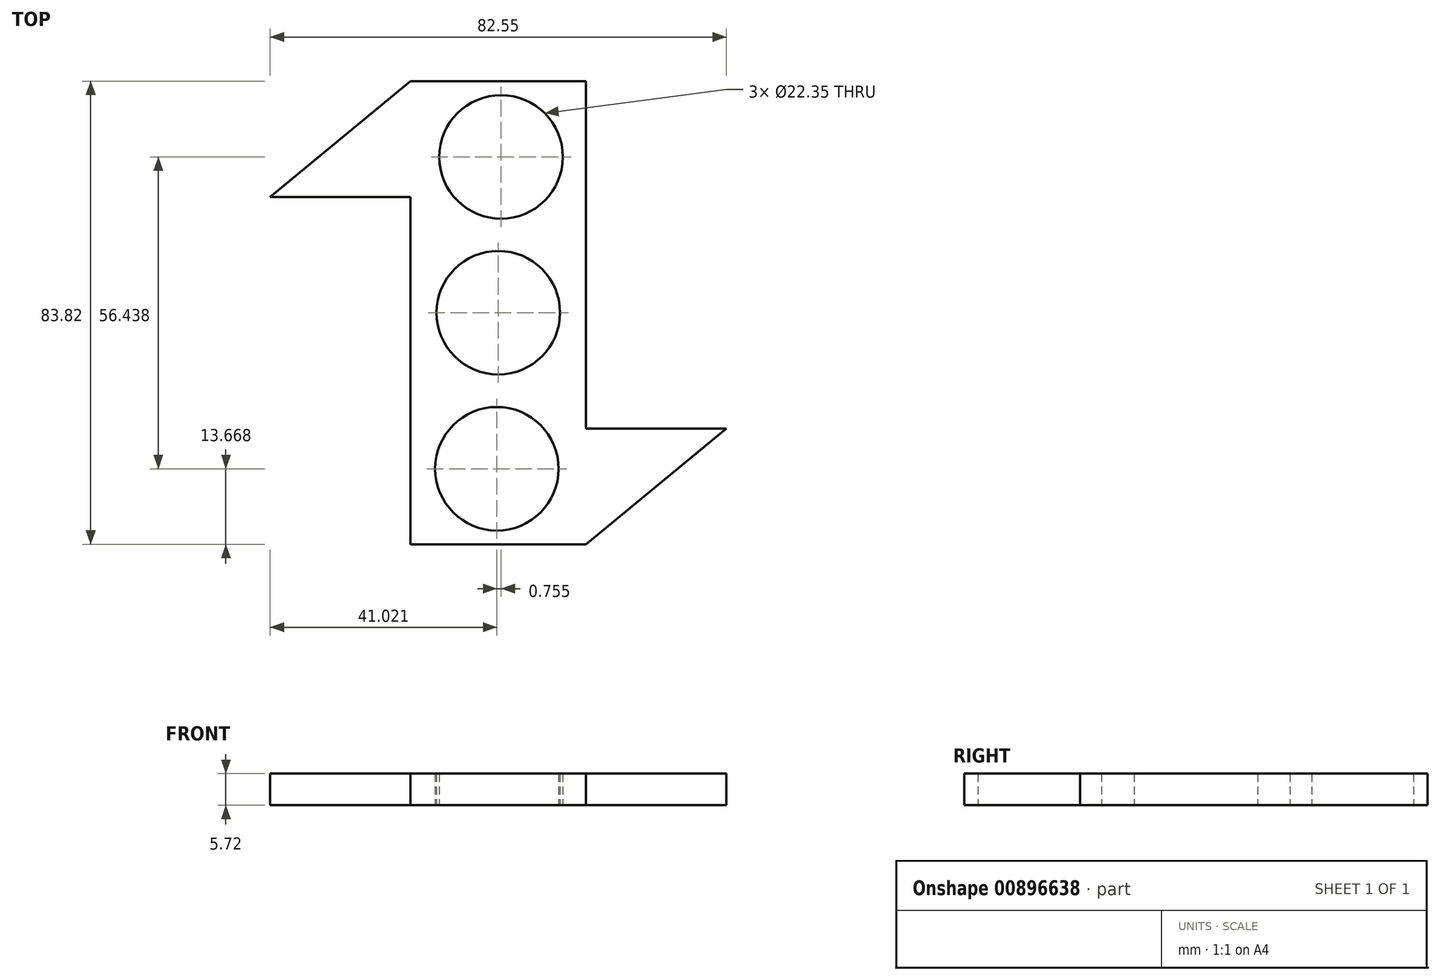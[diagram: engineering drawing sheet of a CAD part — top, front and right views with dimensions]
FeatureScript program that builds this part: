
annotation { "Feature Type Name" : "Feature", "Feature Type Description" : "" }
export const myFeature = defineFeature(function(context is Context, id is Id, definition is map)
    precondition{}
    {
        {
            var Q0;
            Q0=qCreatedBy(makeId("Top.planeOp"),FACE);
            var sketch = newSketch(context, id + "F0", { "sketchPlane" : qUnion([Q0])});
            skCircle(sketch, "E0", {"center": v(-1.1, 0.58) * mm, "radius": 11.18 * mm});
            skCircle(sketch, "E1", {"center": v(-1.1, 0.58) * mm, "radius": 15.88 * mm});
            skLineSegment(sketch, "E2", {"start": v(-16.98, 0.58) * mm, "end": v(-16.98, -41.33) * mm});
            skLineSegment(sketch, "E3", {"start": v(14.77, 0.58) * mm, "end": v(14.77, -41.33) * mm});
            skLineSegment(sketch, "E4", {"start": v(14.77, -41.33) * mm, "end": v(-16.98, -41.33) * mm});
            skLineSegment(sketch, "E5", {"start": v(-16.98, 0.58) * mm, "end": v(-16.98, 42.5) * mm});
            skLineSegment(sketch, "E6", {"start": v(14.77, 0.58) * mm, "end": v(14.77, 42.5) * mm});
            skLineSegment(sketch, "E7", {"start": v(14.77, 42.5) * mm, "end": v(-16.98, 42.5) * mm});
            skCircle(sketch, "E8", {"center": v(-0.6, 28.78) * mm, "radius": 11.18 * mm});
            skCircle(sketch, "E9", {"center": v(-1.36, -27.66) * mm, "radius": 11.18 * mm});
            skLineSegment(sketch, "E10", {"start": v(14.77, -41.33) * mm, "end": v(40.17, -20.37) * mm});
            skPoint(sketch, "E10.endSnap0", {"position": v(14.77, -20.37) * mm});
            skLineSegment(sketch, "E11", {"start": v(40.17, -20.37) * mm, "end": v(14.77, -20.37) * mm});
            skLineSegment(sketch, "E12", {"start": v(-16.98, 42.5) * mm, "end": v(-42.38, 21.54) * mm});
            skPoint(sketch, "E12.endSnap0", {"position": v(14.77, 21.54) * mm});
            skLineSegment(sketch, "E13", {"start": v(-42.38, 21.54) * mm, "end": v(-16.98, 21.54) * mm});
            skSolve(sketch);
        }
        {
            var Q0;
            {var subQ1=sQuery(id+"F0.wireOp",EDGE,"E2");Q0=makeQuery(id+"F0.imprint","IMPRINT",FACE,{"disambiguationData":[TD([[makeQuery(id+"F0.imprint","IMPRINT",EDGE,{"derivedFrom":subQ1}),1.0]])]});}
            var Q1;
            Q1=makeQuery(id+"F0.imprint","IMPRINT",FACE,{"disambiguationData":[TD([[makeQuery(id+"F0.imprint","IMPRINT",EDGE,{"derivedFrom":sQuery(id+"F0.wireOp",EDGE,"E0")}),-1.0]])]});
            var Q2;
            {var subQ1=sQuery(id+"F0.wireOp",EDGE,"E5");Q2=makeQuery(id+"F0.imprint","IMPRINT",FACE,{"disambiguationData":[TD([[makeQuery(id+"F0.imprint","IMPRINT",EDGE,{"derivedFrom":subQ1}),-1.0]])]});}
            var Q3;
            {var subQ0=sQuery(id+"F0.wireOp",EDGE,"E10");Q3=makeQuery(id+"F0.imprint","IMPRINT",FACE,{"disambiguationData":[TD([[makeQuery(id+"F0.imprint","IMPRINT",EDGE,{"derivedFrom":subQ0}),1.0]])]});}
            var Q4;
            {var subQ0=sQuery(id+"F0.wireOp",EDGE,"E12");Q4=makeQuery(id+"F0.imprint","IMPRINT",FACE,{"disambiguationData":[TD([[makeQuery(id+"F0.imprint","IMPRINT",EDGE,{"derivedFrom":subQ0}),1.0]])]});}
            extrude(context, id + "F1", {"entities" : qUnion([Q0, Q1, Q2, Q3, Q4]), "depth" : 5.7 * mm, "offsetDistance" : 25.4 * mm});
        }
    });
